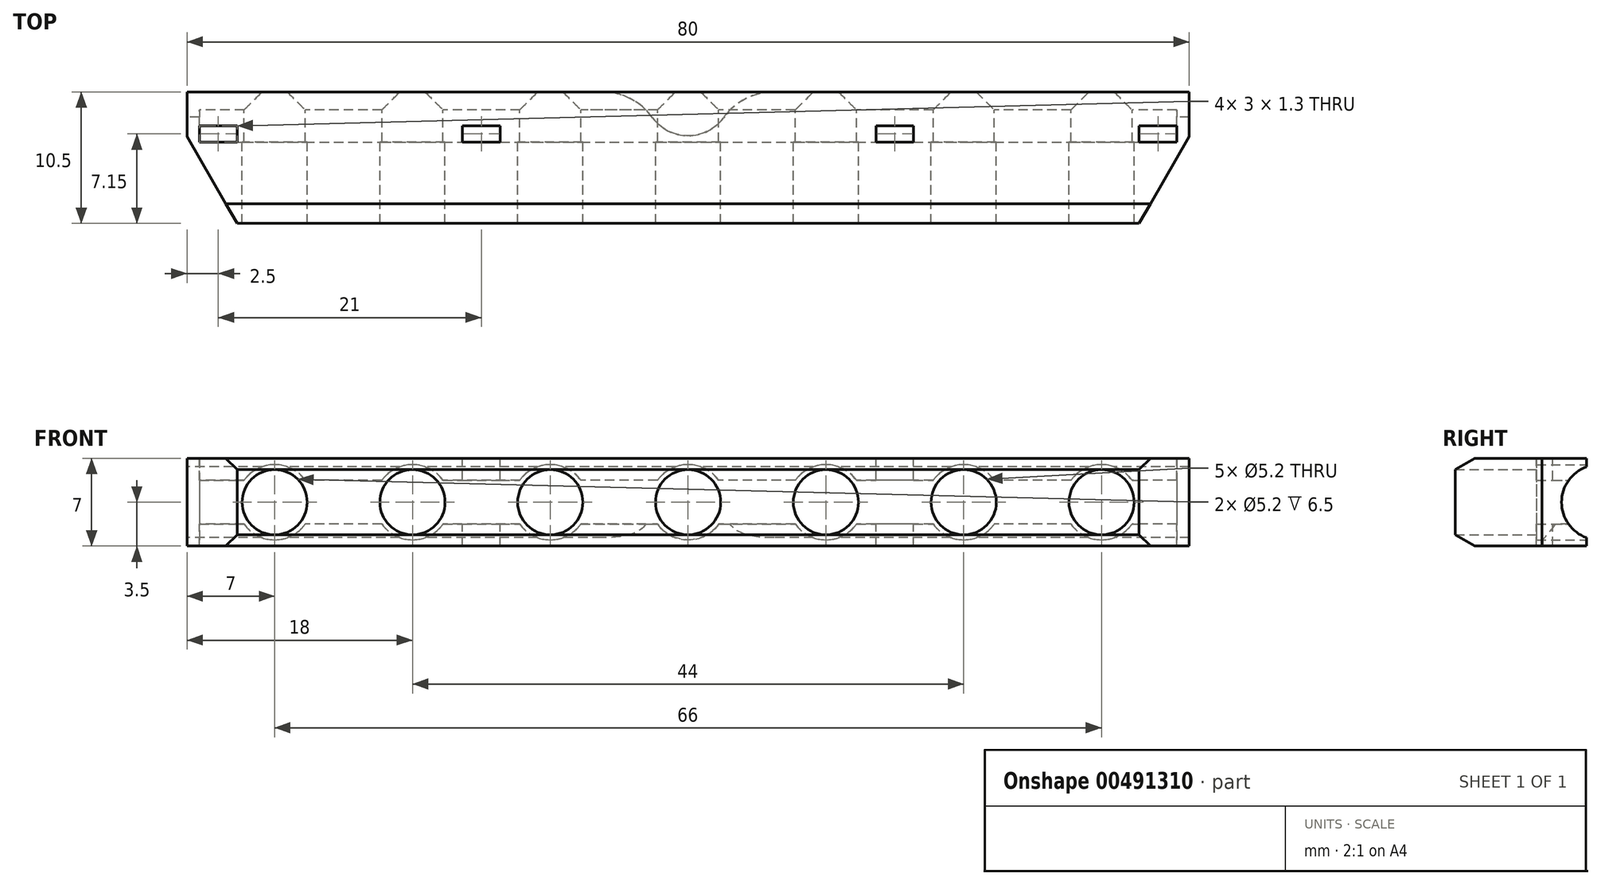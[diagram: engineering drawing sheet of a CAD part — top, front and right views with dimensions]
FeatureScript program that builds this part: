
annotation { "Feature Type Name" : "Feature", "Feature Type Description" : "" }
export const myFeature = defineFeature(function(context is Context, id is Id, definition is map)
    precondition{}
    {
        {
            var Q0;
            Q0=qCreatedBy(makeId("Front.planeOp"),FACE);
            var sketch = newSketch(context, id + "F0", { "sketchPlane" : qUnion([Q0])});
            skLineSegment(sketch, "E0.bottom", {"start": v(40, 3.5) * mm, "end": v(-40, 3.5) * mm});
            skLineSegment(sketch, "E0.top", {"start": v(40, -3.5) * mm, "end": v(-40, -3.5) * mm});
            skLineSegment(sketch, "E0.left", {"start": v(40, 3.5) * mm, "end": v(40, -3.5) * mm});
            skLineSegment(sketch, "E0.right", {"start": v(-40, 3.5) * mm, "end": v(-40, -3.5) * mm});
            skPoint(sketch, "E0.middle", {"position": v(0, 0) * mm});
            skCircle(sketch, "E1", {"center": v(0, 0) * mm, "radius": 2.6 * mm});
            skCircle(sketch, "E2.1.0.0", {"center": v(11, 0) * mm, "radius": 2.6 * mm});
            skCircle(sketch, "E2.2.0.0", {"center": v(22, 0) * mm, "radius": 2.6 * mm});
            skCircle(sketch, "E2.3.0.0", {"center": v(33, 0) * mm, "radius": 2.6 * mm});
            skLineSegment(sketch, "E2.direction1", {"start": v(0, 0) * mm, "end": v(11, 0) * mm, "construction": true});
            skCircle(sketch, "E3.MirrorC", {"center": v(-11, 0) * mm, "radius": 2.6 * mm});
            skCircle(sketch, "E4.MirrorC", {"center": v(-22, 0) * mm, "radius": 2.6 * mm});
            skCircle(sketch, "E5.MirrorC", {"center": v(-33, 0) * mm, "radius": 2.6 * mm});
            skSolve(sketch);
        }
        {
            var Q0;
            Q0 = qSketchRegion(id + "F0", true);
            extrude(context, id + "F1", {"entities" : qUnion([Q0]), "depth" : 11.5 * mm});
        }
        {
            var Q0;
            Q0=makeQuery(id+"F1.opExtrude","CAP_FACE",FACE,{"disambiguationData":[OSD([sQuery(id+"F0.wireOp",EDGE,"E0.bottom"),sQuery(id+"F0.wireOp",EDGE,"E0.top"),sQuery(id+"F0.wireOp",EDGE,"E0.left"),sQuery(id+"F0.wireOp",EDGE,"E0.right"),sQuery(id+"F0.wireOp",EDGE,"E1"),sQuery(id+"F0.wireOp",EDGE,"E2.1.0.0"),sQuery(id+"F0.wireOp",EDGE,"E2.2.0.0"),sQuery(id+"F0.wireOp",EDGE,"E2.3.0.0"),sQuery(id+"F0.wireOp",EDGE,"E3.MirrorC"),sQuery(id+"F0.wireOp",EDGE,"E4.MirrorC"),sQuery(id+"F0.wireOp",EDGE,"E5.MirrorC")])],"isStart":true});
            var sketch = newSketch(context, id + "F2", { "sketchPlane" : qUnion([Q0])});
            skCircle(sketch, "E6", {"center": v(0, 0) * mm, "radius": 3 * mm});
            skCircle(sketch, "E7.1.0.0", {"center": v(11, 0) * mm, "radius": 3 * mm});
            skCircle(sketch, "E7.2.0.0", {"center": v(22, 0) * mm, "radius": 3 * mm});
            skCircle(sketch, "E7.3.0.0", {"center": v(33, 0) * mm, "radius": 3 * mm});
            skLineSegment(sketch, "E7.direction1", {"start": v(0, 0) * mm, "end": v(11, 0) * mm, "construction": true});
            skCircle(sketch, "E8.MirrorC", {"center": v(-11, 0) * mm, "radius": 3 * mm});
            skCircle(sketch, "E9.MirrorC", {"center": v(-22, 0) * mm, "radius": 3 * mm});
            skCircle(sketch, "E10.MirrorC", {"center": v(-33, 0) * mm, "radius": 3 * mm});
            skSolve(sketch);
        }
        {
            var Q0;
            Q0 = qSketchRegion(id + "F2", true);
            extrude(context, id + "F3", {"entities" : qUnion([Q0]), "operationType" : NewBodyOperationType.REMOVE, "oppositeDirection" : true, "depth" : 5 * mm});
        }
        {
            var Q0;
            Q0=makeQuery(id+"F1.opExtrude","SWEPT_FACE",FACE,{"disambiguationData":[OSD([sQuery(id+"F0.wireOp",EDGE,"E0.right")])]});
            var sketch = newSketch(context, id + "F4", { "sketchPlane" : qUnion([Q0])});
            skCircle(sketch, "E11", {"center": v(0, 0) * mm, "radius": 3 * mm});
            skPoint(sketch, "E12.middle", {"position": v(3, 0) * mm});
            skSolve(sketch);
        }
        {
            var Q0;
            Q0 = qSketchRegion(id + "F4", true);
            extrude(context, id + "F5", {"entities" : qUnion([Q0]), "operationType" : NewBodyOperationType.REMOVE, "endBound" : BoundingType.THROUGH_ALL, "oppositeDirection" : true, "depth" : 25 * mm});
        }
        {
            var Q0;
            Q0=qCreatedBy(makeId("Right.planeOp"),FACE);
            var sketch = newSketch(context, id + "F6", { "sketchPlane" : qUnion([Q0])});
            skCircle(sketch, "E13.0", {"center": v(0, 0) * mm, "radius": 3 * mm, "construction": true});
            skLineSegment(sketch, "E14.bottom", {"start": v(-5, 1.75) * mm, "end": v(-1, 1.75) * mm});
            skLineSegment(sketch, "E14.top", {"start": v(-5, -1.75) * mm, "end": v(-1, -1.75) * mm});
            skLineSegment(sketch, "E14.left", {"start": v(-5, 1.75) * mm, "end": v(-5, -1.75) * mm});
            skLineSegment(sketch, "E14.right", {"start": v(-1, 1.75) * mm, "end": v(-1, -1.75) * mm});
            skPoint(sketch, "E14.middle", {"position": v(-3, 0) * mm});
            skSolve(sketch);
        }
        {
            var Q0;
            Q0 = qSketchRegion(id + "F6", true);
            extrude(context, id + "F7", {"entities" : qUnion([Q0]), "operationType" : NewBodyOperationType.REMOVE, "oppositeDirection" : true, "depth" : 39 * mm, "hasSecondDirection" : true, "secondDirectionOppositeDirection" : false, "secondDirectionDepth" : 39 * mm});
        }
        {
            var Q0;
            Q0=makeQuery(id+"F1.opExtrude","CAP_EDGE",EDGE,{"disambiguationData":[OSD([sQuery(id+"F0.wireOp",EDGE,"E0.right")])],"isStart":false});
            var Q1;
            Q1=makeQuery(id+"F1.opExtrude","CAP_EDGE",EDGE,{"disambiguationData":[OSD([sQuery(id+"F0.wireOp",EDGE,"E0.left")])],"isStart":false});
            chamfer(context, id + "F8", {"entities" : qUnion([Q0, Q1]), "chamferType" : ChamferType.OFFSET_ANGLE, "width" : 4 * mm, "oppositeDirection" : false, "angle" : 60 * degree, "tangentPropagation" : true});
        }
        {
            var Q0;
            Q0=makeQuery(id+"F1.opExtrude","CAP_EDGE",EDGE,{"disambiguationData":[OSD([sQuery(id+"F0.wireOp",EDGE,"E0.bottom")])],"isStart":false});
            var Q1;
            Q1=makeQuery(id+"F1.opExtrude","CAP_EDGE",EDGE,{"disambiguationData":[OSD([sQuery(id+"F0.wireOp",EDGE,"E0.top")])],"isStart":false});
            chamfer(context, id + "F9", {"entities" : qUnion([Q0, Q1]), "chamferType" : ChamferType.OFFSET_ANGLE, "width" : .9 * mm, "oppositeDirection" : false, "angle" : 60 * degree, "tangentPropagation" : true});
        }
        {
            var Q0;
            Q0=makeQuery(id+"F1.opExtrude","SWEPT_FACE",FACE,{"disambiguationData":[OSD([sQuery(id+"F0.wireOp",EDGE,"E0.right")])]});
            var sketch = newSketch(context, id + "F10", { "sketchPlane" : qUnion([Q0])});
            skLineSegment(sketch, "E15.bottom", {"start": v(1, 5.16) * mm, "end": v(-1, 5.16) * mm});
            skLineSegment(sketch, "E15.top", {"start": v(1, -5.16) * mm, "end": v(-1, -5.16) * mm});
            skLineSegment(sketch, "E15.left", {"start": v(1, 5.16) * mm, "end": v(1, -5.16) * mm});
            skLineSegment(sketch, "E15.right", {"start": v(-1, 5.16) * mm, "end": v(-1, -5.16) * mm});
            skPoint(sketch, "E15.middle", {"position": v(0, 0) * mm});
            skSolve(sketch);
        }
        {
            var Q0;
            Q0 = qSketchRegion(id + "F10", true);
            extrude(context, id + "F11", {"entities" : qUnion([Q0]), "operationType" : NewBodyOperationType.REMOVE, "endBound" : BoundingType.THROUGH_ALL, "oppositeDirection" : true, "depth" : 25 * mm});
        }
        {
            var Q0;
            Q0=makeQuery(id+"F1.opExtrude","SWEPT_FACE",FACE,{"disambiguationData":[OSD([sQuery(id+"F0.wireOp",EDGE,"E0.top")])]});
            var sketch = newSketch(context, id + "F12", { "sketchPlane" : qUnion([Q0])});
            skCircle(sketch, "E16", {"center": v(0, 1) * mm, "radius": 3.5 * mm});
            skSolve(sketch);
        }
        {
            var Q0;
            Q0 = qSketchRegion(id + "F12", true);
            var Q1;
            {var subQ0=sQuery(id+"F2.wireOp",EDGE,"E8.MirrorC");var subQ1=sQuery(id+"F2.wireOp",EDGE,"E6");var subQ2=makeQuery(id+"F3.boolean.opBoolean","COPY",FACE,{"derivedFrom":makeQuery(id+"F3.opExtrude","SWEPT_FACE",FACE,{"disambiguationData":[OSD([subQ1])]})});var subQ3=makeQuery(id+"F3.boolean.opBoolean","COPY",FACE,{"derivedFrom":makeQuery(id+"F3.opExtrude","SWEPT_FACE",FACE,{"disambiguationData":[OSD([subQ0])]})});var subQ4=makeQuery(id+"F5.opExtrude","SWEPT_FACE",FACE,{"disambiguationData":[OSD([sQuery(id+"F4.wireOp",EDGE,"E11")])]});Q1=makeQuery(id+"F7.boolean.opBoolean","COPY",FACE,{"disambiguationData":[TD([makeQuery(id+"F5.boolean.opBoolean","COPY",FACE,{"disambiguationData":[TD([makeQuery(id+"F1.opExtrude","CAP_FACE",FACE,{"disambiguationData":[OSD([sQuery(id+"F0.wireOp",EDGE,"E0.bottom"),sQuery(id+"F0.wireOp",EDGE,"E0.top"),sQuery(id+"F0.wireOp",EDGE,"E0.left"),sQuery(id+"F0.wireOp",EDGE,"E0.right"),sQuery(id+"F0.wireOp",EDGE,"E1"),sQuery(id+"F0.wireOp",EDGE,"E2.1.0.0"),sQuery(id+"F0.wireOp",EDGE,"E2.2.0.0"),sQuery(id+"F0.wireOp",EDGE,"E2.3.0.0"),sQuery(id+"F0.wireOp",EDGE,"E3.MirrorC"),sQuery(id+"F0.wireOp",EDGE,"E4.MirrorC"),sQuery(id+"F0.wireOp",EDGE,"E5.MirrorC")])],"isStart":true}),subQ2,subQ3,subQ4])],"derivedFrom":subQ4})])],"derivedFrom":makeQuery(id+"F7.opExtrude","SWEPT_FACE",FACE,{"disambiguationData":[OSD([sQuery(id+"F6.wireOp",EDGE,"E14.top")])]})});}
            extrude(context, id + "F13", {"entities" : qUnion([Q0]), "operationType" : NewBodyOperationType.REMOVE, "endBound" : BoundingType.UP_TO_SURFACE, "oppositeDirection" : true, "endBoundEntityFace" : qUnion([Q1]), "depth" : 25 * mm});
        }
        {
            var Q0;
            {var subQ4=sQuery(id+"F0.wireOp",EDGE,"E0.top");Q0=makeQuery(id+"F13.boolean.opBoolean","INTERSECT",EDGE,{"disambiguationData":[OD(1.0)],"derivedFrom":[makeQuery(id+"F11.boolean.opBoolean","COPY",FACE,{"disambiguationData":[TD([makeQuery(id+"F1.opExtrude","SWEPT_FACE",FACE,{"disambiguationData":[OSD([subQ4])]})])],"derivedFrom":makeQuery(id+"F11.opExtrude","SWEPT_FACE",FACE,{"disambiguationData":[OSD([sQuery(id+"F10.wireOp",EDGE,"E15.left")])]})}),makeQuery(id+"F13.opExtrude","SWEPT_FACE",FACE,{"disambiguationData":[OSD([sQuery(id+"F12.wireOp",EDGE,"E16")])]})]});}
            var Q1;
            {var subQ4=sQuery(id+"F0.wireOp",EDGE,"E0.top");Q1=makeQuery(id+"F13.boolean.opBoolean","INTERSECT",EDGE,{"disambiguationData":[OD(0.0)],"derivedFrom":[makeQuery(id+"F11.boolean.opBoolean","COPY",FACE,{"disambiguationData":[TD([makeQuery(id+"F1.opExtrude","SWEPT_FACE",FACE,{"disambiguationData":[OSD([subQ4])]})])],"derivedFrom":makeQuery(id+"F11.opExtrude","SWEPT_FACE",FACE,{"disambiguationData":[OSD([sQuery(id+"F10.wireOp",EDGE,"E15.left")])]})}),makeQuery(id+"F13.opExtrude","SWEPT_FACE",FACE,{"disambiguationData":[OSD([sQuery(id+"F12.wireOp",EDGE,"E16")])]})]});}
            fillet(context, id + "F14", {"entities" : qUnion([Q0, Q1]), "radius" : 5 * mm, "tangentPropagation" : true, "allowEdgeOverflow" : false});
        }
        {
            var Q0;
            Q0=makeQuery(id+"F1.opExtrude","SWEPT_FACE",FACE,{"disambiguationData":[OSD([sQuery(id+"F0.wireOp",EDGE,"E0.bottom")])]});
            var sketch = newSketch(context, id + "F15", { "sketchPlane" : qUnion([Q0])});
            skLineSegment(sketch, "E17", {"start": v(0, -1) * mm, "end": v(36, -1) * mm, "construction": true});
            skLineSegment(sketch, "E18", {"start": v(36, -1) * mm, "end": v(36, -3.7) * mm, "construction": true});
            skLineSegment(sketch, "E19.bottom", {"start": v(36, -3.7) * mm, "end": v(39, -3.7) * mm});
            skLineSegment(sketch, "E19.top", {"start": v(36, -5) * mm, "end": v(39, -5) * mm});
            skLineSegment(sketch, "E19.left", {"start": v(36, -3.7) * mm, "end": v(36, -5) * mm});
            skLineSegment(sketch, "E19.right", {"start": v(39, -3.7) * mm, "end": v(39, -5) * mm});
            skLineSegment(sketch, "E20.1.0.0", {"start": v(15, -3.7) * mm, "end": v(18, -3.7) * mm});
            skLineSegment(sketch, "E20.1.0.1", {"start": v(15, -5) * mm, "end": v(18, -5) * mm});
            skLineSegment(sketch, "E20.1.0.2", {"start": v(15, -3.7) * mm, "end": v(15, -5) * mm});
            skLineSegment(sketch, "E20.1.0.3", {"start": v(18, -3.7) * mm, "end": v(18, -5) * mm});
            skLineSegment(sketch, "E20.direction1", {"start": v(36, -3.7) * mm, "end": v(15, -3.7) * mm, "construction": true});
            skLineSegment(sketch, "E21.MirrorCS", {"start": v(-18, -3.7) * mm, "end": v(-18, -5) * mm});
            skLineSegment(sketch, "E22.MirrorCS", {"start": v(-15, -5) * mm, "end": v(-18, -5) * mm});
            skLineSegment(sketch, "E23.MirrorCS", {"start": v(-15, -3.7) * mm, "end": v(-15, -5) * mm});
            skLineSegment(sketch, "E24.MirrorCS", {"start": v(-15, -3.7) * mm, "end": v(-18, -3.7) * mm});
            skLineSegment(sketch, "E25.MirrorCS", {"start": v(-36, -3.7) * mm, "end": v(-39, -3.7) * mm});
            skLineSegment(sketch, "E26.MirrorCS", {"start": v(-36, -3.7) * mm, "end": v(-36, -5) * mm});
            skLineSegment(sketch, "E27.MirrorCS", {"start": v(-36, -5) * mm, "end": v(-39, -5) * mm});
            skLineSegment(sketch, "E28.MirrorCS", {"start": v(-39, -3.7) * mm, "end": v(-39, -5) * mm});
            skSolve(sketch);
        }
        {
            var Q0;
            Q0 = qSketchRegion(id + "F15", true);
            extrude(context, id + "F16", {"entities" : qUnion([Q0]), "operationType" : NewBodyOperationType.REMOVE, "endBound" : BoundingType.THROUGH_ALL, "oppositeDirection" : true, "depth" : 25 * mm});
        }
    });
